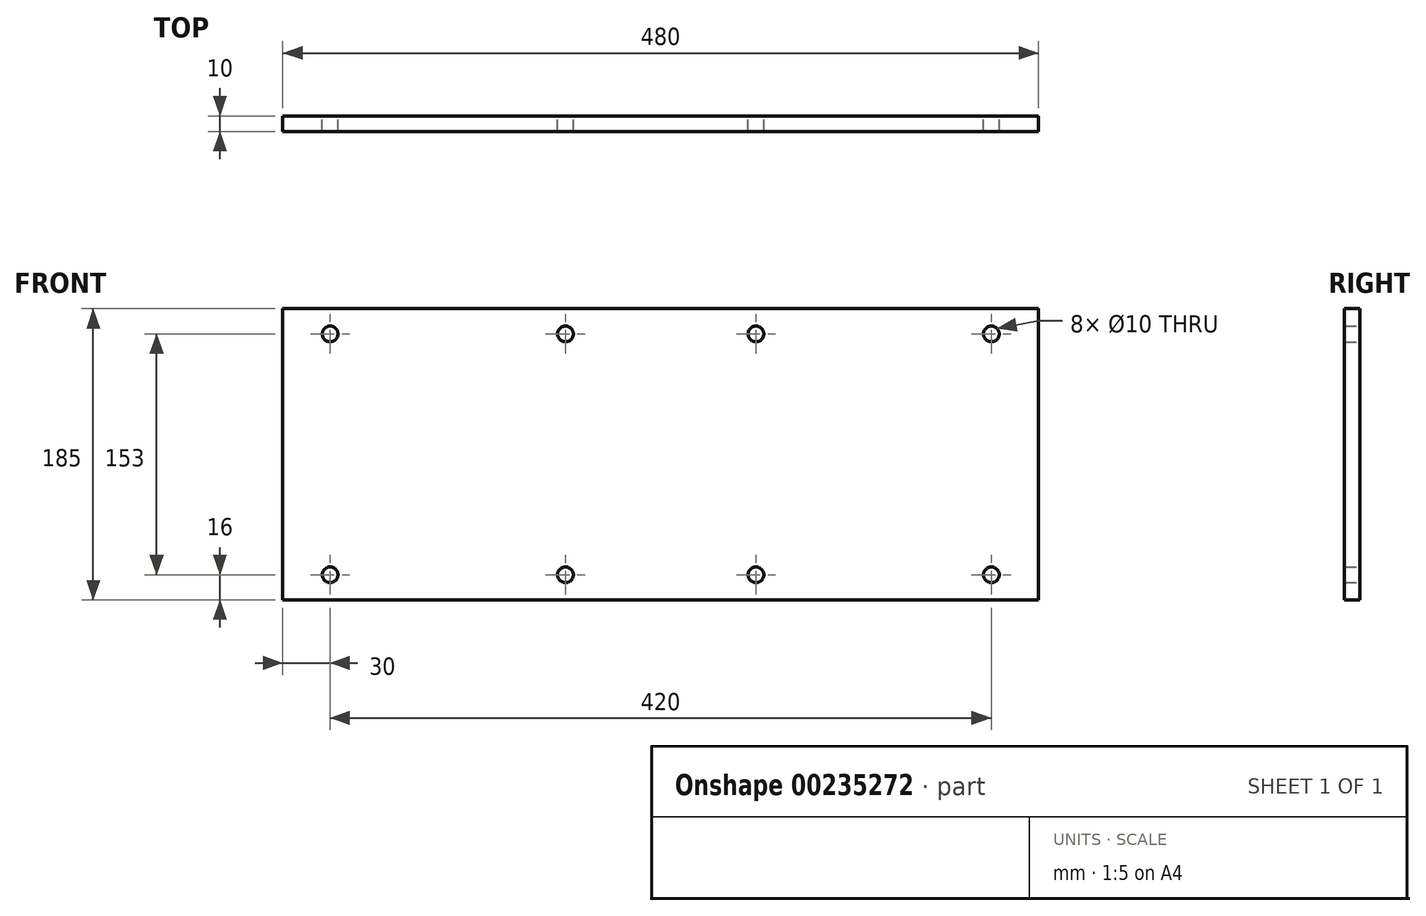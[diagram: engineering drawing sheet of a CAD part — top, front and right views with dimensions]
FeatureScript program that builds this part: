
annotation { "Feature Type Name" : "Feature", "Feature Type Description" : "" }
export const myFeature = defineFeature(function(context is Context, id is Id, definition is map)
    precondition{}
    {
        {
            var Q0;
            Q0=qCreatedBy(makeId("Front.planeOp"),FACE);
            var sketch = newSketch(context, id + "F0", { "sketchPlane" : qUnion([Q0]), "disableImprinting" : false});
            skLineSegment(sketch, "E0.bottom", {"start": v(240, 92.5) * mm, "end": v(-240, 92.5) * mm});
            skLineSegment(sketch, "E0.top", {"start": v(240, -92.5) * mm, "end": v(-240, -92.5) * mm});
            skLineSegment(sketch, "E0.left", {"start": v(240, 92.5) * mm, "end": v(240, -92.5) * mm});
            skLineSegment(sketch, "E0.right", {"start": v(-240, 92.5) * mm, "end": v(-240, -92.5) * mm});
            skPoint(sketch, "E0.middle", {"position": v(0, 0) * mm});
            skCircle(sketch, "E1", {"center": v(-210, 76.5) * mm, "radius": 5 * mm});
            skCircle(sketch, "E2", {"center": v(-210, -76.5) * mm, "radius": 5 * mm});
            skCircle(sketch, "E3", {"center": v(210, -76.5) * mm, "radius": 5 * mm});
            skCircle(sketch, "E4", {"center": v(60.5, 76.5) * mm, "radius": 5 * mm});
            skCircle(sketch, "E5", {"center": v(-60.5, -76.5) * mm, "radius": 5 * mm});
            skCircle(sketch, "E6", {"center": v(-60.5, 76.5) * mm, "radius": 5 * mm});
            skCircle(sketch, "E7", {"center": v(210, 76.5) * mm, "radius": 5 * mm});
            skCircle(sketch, "E8", {"center": v(60.5, -76.5) * mm, "radius": 5 * mm});
            skSolve(sketch);
        }
        {
            var Q0;
            Q0=makeQuery(id+"F0.imprint","IMPRINT",FACE,{"disambiguationData":[TD([[makeQuery(id+"F0.imprint","IMPRINT",EDGE,{"derivedFrom":sQuery(id+"F0.wireOp",EDGE,"E0.bottom")}),1.0]])]});
            extrude(context, id + "F1", {"entities" : qUnion([Q0]), "depth" : 10 * mm});
        }
    });
